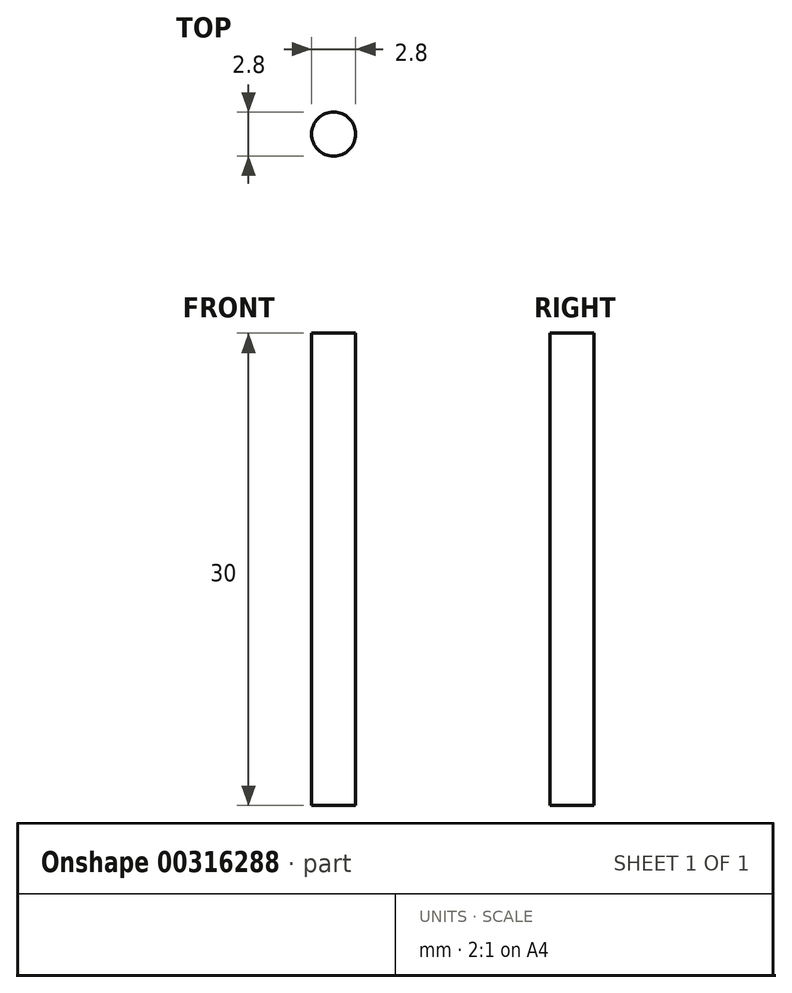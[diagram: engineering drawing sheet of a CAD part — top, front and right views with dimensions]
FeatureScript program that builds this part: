
annotation { "Feature Type Name" : "Feature", "Feature Type Description" : "" }
export const myFeature = defineFeature(function(context is Context, id is Id, definition is map)
    precondition{}
    {
        {
            var Q0;
            Q0=qCreatedBy(makeId("Top.planeOp"),FACE);
            var sketch = newSketch(context, id + "F0", { "sketchPlane" : qUnion([Q0])});
            skCircle(sketch, "E0", {"center": v(0, 0) * mm, "radius": 1.4 * mm});
            skSolve(sketch);
        }
        {
            var Q0;
            Q0=makeQuery(id+"F0.imprint","IMPRINT",FACE,{"disambiguationData":[TD([[makeQuery(id+"F0.imprint","IMPRINT",EDGE,{"derivedFrom":sQuery(id+"F0.wireOp",EDGE,"E0")}),1.0]])]});
            extrude(context, id + "F1", {"entities" : qUnion([Q0]), "depth" : 30 * mm});
        }
    });
